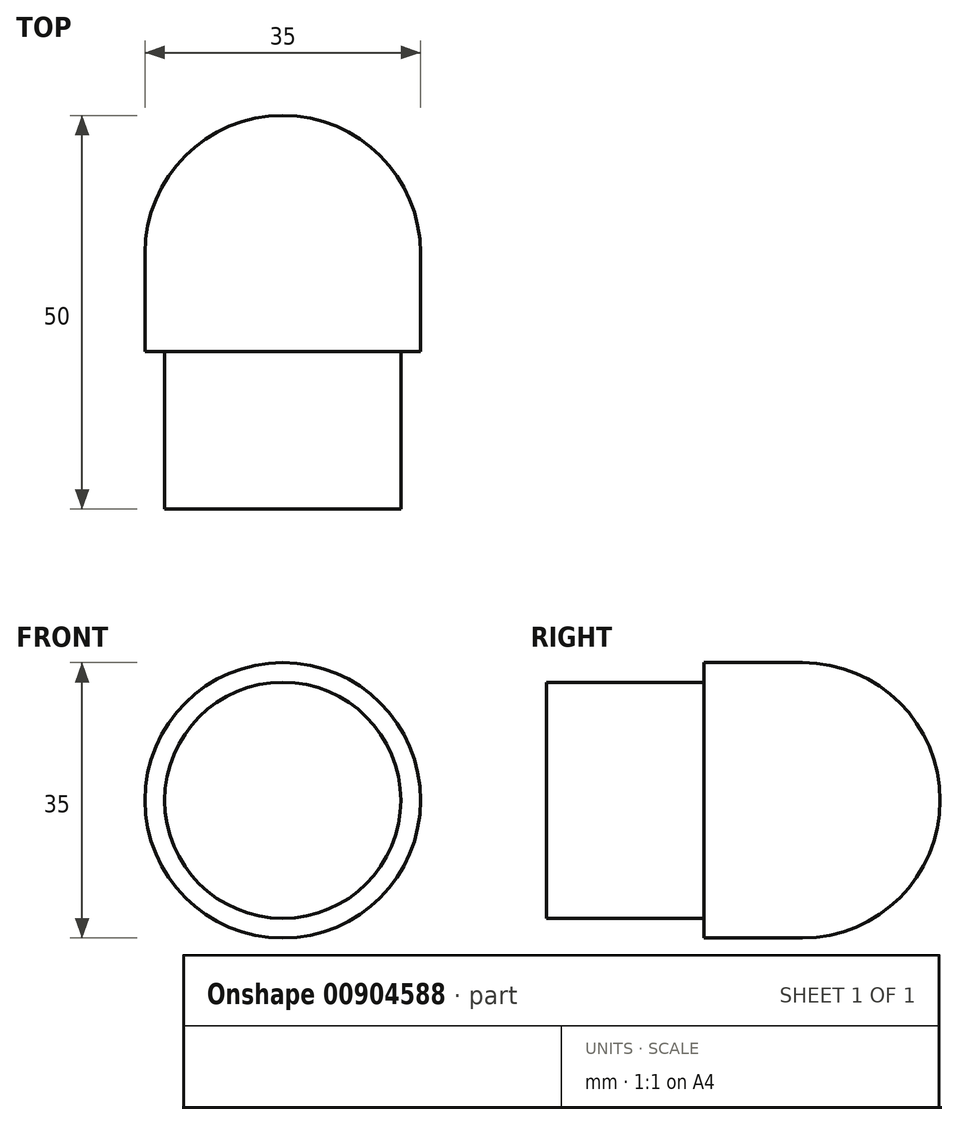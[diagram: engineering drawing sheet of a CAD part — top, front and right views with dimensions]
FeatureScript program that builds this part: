
annotation { "Feature Type Name" : "Feature", "Feature Type Description" : "" }
export const myFeature = defineFeature(function(context is Context, id is Id, definition is map)
    precondition{}
    {
        {
            var Q0;
            Q0=qCreatedBy(makeId("Front.planeOp"),FACE);
            var sketch = newSketch(context, id + "F0", { "sketchPlane" : qUnion([Q0])});
            skCircle(sketch, "E0", {"center": v(0, 0) * mm, "radius": 15 * mm});
            skSolve(sketch);
        }
        {
            var Q0;
            Q0=makeQuery(id+"F0.imprint","IMPRINT",FACE,{"disambiguationData":[TD([[makeQuery(id+"F0.imprint","IMPRINT",EDGE,{"derivedFrom":sQuery(id+"F0.wireOp",EDGE,"E0")}),1.0]])]});
            extrude(context, id + "F1", {"entities" : qUnion([Q0]), "depth" : 20 * mm, "offsetDistance" : 25.4 * mm});
        }
        {
            var Q0;
            Q0=makeQuery(id+"F1.opExtrude","CAP_FACE",FACE,{"disambiguationData":[OSD([sQuery(id+"F0.wireOp",EDGE,"E0")])],"isStart":true});
            var sketch = newSketch(context, id + "F2", { "sketchPlane" : qUnion([Q0])});
            skCircle(sketch, "E1", {"center": v(0, 0) * mm, "radius": 17.5 * mm});
            skSolve(sketch);
        }
        {
            var Q0;
            Q0=makeQuery(id+"F2.imprint","IMPRINT",FACE,{"disambiguationData":[TD([[makeQuery(id+"F2.imprint","IMPRINT",EDGE,{"derivedFrom":sQuery(id+"F2.wireOp",EDGE,"E1")}),1.0]])]});
            var Q1;
            Q1=makeQuery(id+"F2.imprint","IMPRINT",FACE,{"disambiguationData":[TD([[makeQuery(id+"F2.imprint","IMPRINT",EDGE,{"derivedFrom":makeQuery(id+"F1.opExtrude","CAP_EDGE",EDGE,{"disambiguationData":[OSD([sQuery(id+"F0.wireOp",EDGE,"E0")])],"isStart":true})}),-1.0]])]});
            extrude(context, id + "F3", {"entities" : qUnion([Q0, Q1]), "operationType" : NewBodyOperationType.ADD, "depth" : 12.5 * mm, "offsetDistance" : 25.4 * mm});
        }
        {
            var Q0;
            Q0=makeQuery(id+"F3.opExtrude","CAP_FACE",FACE,{"disambiguationData":[OSD([sQuery(id+"F2.wireOp",EDGE,"E1")])],"isStart":false});
            var sketch = newSketch(context, id + "F4", { "sketchPlane" : qUnion([Q0])});
            skLineSegment(sketch, "E2", {"start": v(0, 17.5) * mm, "end": v(0, -17.5) * mm});
            skSolve(sketch);
        }
        {
            var Q0;
            {var subQ0=sQuery(id+"F4.wireOp",EDGE,"E2");Q0=makeQuery(id+"F4.imprint","IMPRINT",FACE,{"disambiguationData":[TD([[makeQuery(id+"F4.imprint","IMPRINT",EDGE,{"derivedFrom":subQ0}),1.0]])]});}
            var Q1;
            Q1=sQuery(id+"F4.wireOp",EDGE,"E2");
            revolve(context, id + "F5", {"operationType" : NewBodyOperationType.ADD, "surfaceOperationType" : NewSurfaceOperationType.NEW, "entities" : qUnion([Q0]), "axis" : qUnion([Q1]), "revolveType" : RevolveType.FULL});
        }
    });
